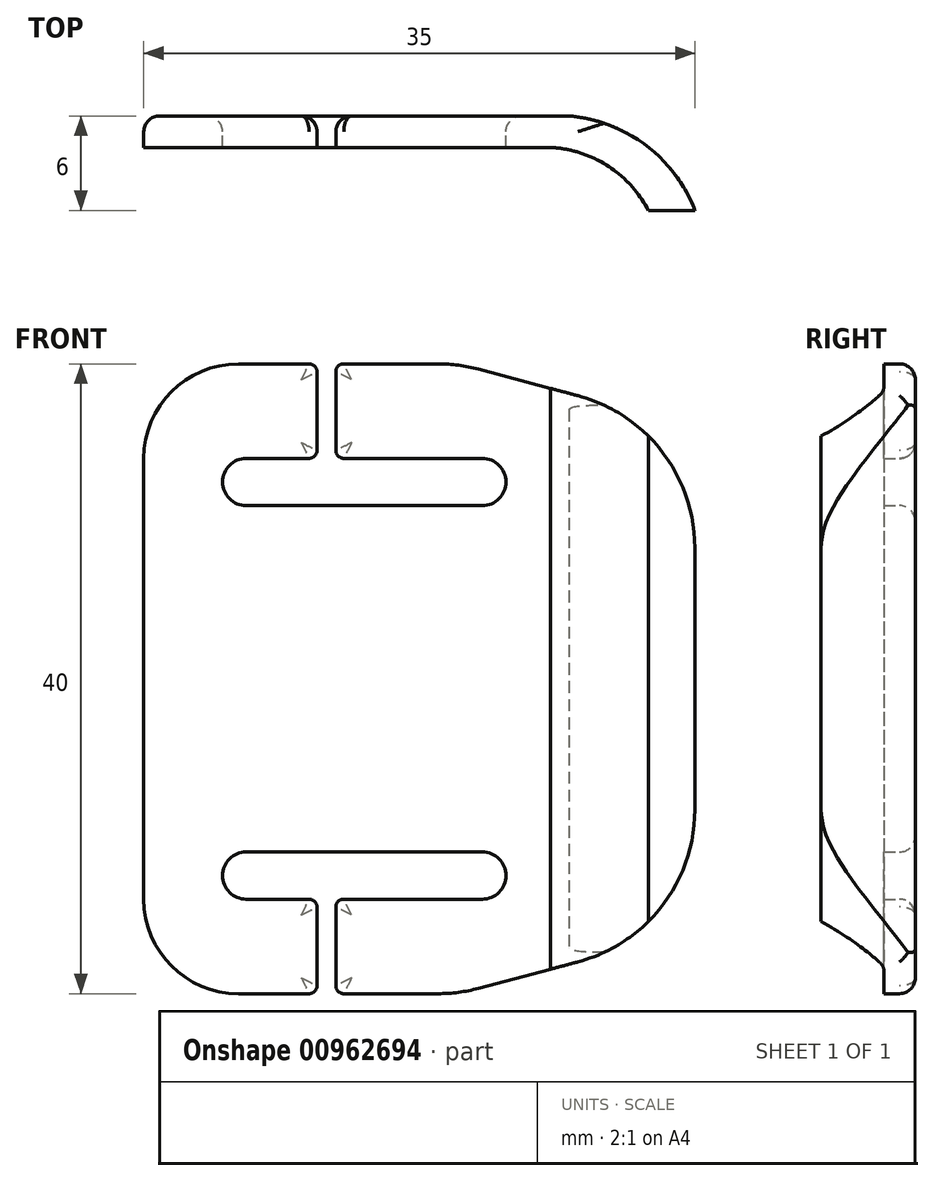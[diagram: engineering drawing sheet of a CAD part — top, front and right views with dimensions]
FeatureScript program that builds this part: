
annotation { "Feature Type Name" : "Feature", "Feature Type Description" : "" }
export const myFeature = defineFeature(function(context is Context, id is Id, definition is map)
    precondition{}
    {
        {
            var Q0;
            Q0=qCreatedBy(makeId("Front.planeOp"),FACE);
            var sketch = newSketch(context, id + "F0", { "sketchPlane" : qUnion([Q0])});
            skLineSegment(sketch, "E0.bottom", {"start": v(1, -20) * mm, "end": v(5.5, -20) * mm});
            skLineSegment(sketch, "E0.top", {"start": v(1, 20) * mm, "end": v(5.5, 20) * mm});
            skLineSegment(sketch, "E0.left", {"start": v(-5, -14) * mm, "end": v(-5, 14) * mm});
            skLineSegment(sketch, "E0.right", {"start": v(30, -8.32) * mm, "end": v(30, 8.32) * mm});
            skLineSegment(sketch, "E1.bottom", {"start": v(1.5, 14) * mm, "end": v(5.5, 14) * mm});
            skLineSegment(sketch, "E1.top", {"start": v(1.5, 11) * mm, "end": v(16.5, 11) * mm});
            skLineSegment(sketch, "E1.left", {"start": v(0, 12.5) * mm, "end": v(0, 12.5) * mm});
            skLineSegment(sketch, "E1.right", {"start": v(18, 12.5) * mm, "end": v(18, 12.5) * mm});
            skLineSegment(sketch, "E2.bottom", {"start": v(1.5, -11) * mm, "end": v(16.5, -11) * mm});
            skLineSegment(sketch, "E2.top", {"start": v(1.5, -14) * mm, "end": v(5.5, -14) * mm});
            skLineSegment(sketch, "E2.left", {"start": v(0, -12.5) * mm, "end": v(0, -12.5) * mm});
            skLineSegment(sketch, "E2.right", {"start": v(18, -12.5) * mm, "end": v(18, -12.5) * mm});
            skPoint(sketch, "E3.visualSharp", {"position": v(-5, 20) * mm});
            skArc(sketch, "E3.filletArc", {"start": v(1, 20) * mm, "mid": v(-3.24, 18.24) * mm, "end": v(-5, 14) * mm});
            skPoint(sketch, "E4.visualSharp", {"position": v(-5, -20) * mm});
            skArc(sketch, "E4.filletArc", {"start": v(-5, -14) * mm, "mid": v(-3.24, -18.24) * mm, "end": v(1, -20) * mm});
            skLineSegment(sketch, "E5", {"start": v(6, 19.5) * mm, "end": v(6, 14.5) * mm});
            skLineSegment(sketch, "E6", {"start": v(7.2, 19.5) * mm, "end": v(7.2, 14.5) * mm});
            skLineSegment(sketch, "E7.trimOffspring", {"start": v(6, -14.5) * mm, "end": v(6, -19.5) * mm});
            skLineSegment(sketch, "E8.trimOffspring", {"start": v(7.2, -14.5) * mm, "end": v(7.2, -19.5) * mm});
            skLineSegment(sketch, "E9.trimOffspring", {"start": v(7.7, -20) * mm, "end": v(13.69, -20) * mm});
            skLineSegment(sketch, "E10.trimOffspring", {"start": v(7.7, -14) * mm, "end": v(16.5, -14) * mm});
            skLineSegment(sketch, "E11.trimOffspring", {"start": v(7.7, 14) * mm, "end": v(16.5, 14) * mm});
            skLineSegment(sketch, "E12.trimOffspring", {"start": v(7.7, 20) * mm, "end": v(13.69, 20) * mm});
            skPoint(sketch, "E13.visualSharp", {"position": v(0, 14) * mm});
            skArc(sketch, "E13.filletArc", {"start": v(1.5, 14) * mm, "mid": v(0.44, 13.56) * mm, "end": v(0, 12.5) * mm});
            skPoint(sketch, "E14.visualSharp", {"position": v(0, 11) * mm});
            skArc(sketch, "E14.filletArc", {"start": v(0, 12.5) * mm, "mid": v(0.44, 11.44) * mm, "end": v(1.5, 11) * mm});
            skPoint(sketch, "E15.visualSharp", {"position": v(18, 14) * mm});
            skArc(sketch, "E15.filletArc", {"start": v(18, 12.5) * mm, "mid": v(17.56, 13.56) * mm, "end": v(16.5, 14) * mm});
            skPoint(sketch, "E16.visualSharp", {"position": v(18, 11) * mm});
            skArc(sketch, "E16.filletArc", {"start": v(16.5, 11) * mm, "mid": v(17.56, 11.44) * mm, "end": v(18, 12.5) * mm});
            skPoint(sketch, "E17.visualSharp", {"position": v(0, -11) * mm});
            skArc(sketch, "E17.filletArc", {"start": v(1.5, -11) * mm, "mid": v(0.44, -11.44) * mm, "end": v(0, -12.5) * mm});
            skPoint(sketch, "E18.visualSharp", {"position": v(0, -14) * mm});
            skArc(sketch, "E18.filletArc", {"start": v(0, -12.5) * mm, "mid": v(0.44, -13.56) * mm, "end": v(1.5, -14) * mm});
            skPoint(sketch, "E19.visualSharp", {"position": v(18, -11) * mm});
            skArc(sketch, "E19.filletArc", {"start": v(18, -12.5) * mm, "mid": v(17.56, -11.44) * mm, "end": v(16.5, -11) * mm});
            skPoint(sketch, "E20.visualSharp", {"position": v(18, -14) * mm});
            skArc(sketch, "E20.filletArc", {"start": v(16.5, -14) * mm, "mid": v(17.56, -13.56) * mm, "end": v(18, -12.5) * mm});
            skPoint(sketch, "E21.visualSharp", {"position": v(6, 14) * mm});
            skArc(sketch, "E21.filletArc", {"start": v(5.5, 14) * mm, "mid": v(5.85, 14.15) * mm, "end": v(6, 14.5) * mm});
            skPoint(sketch, "E22.visualSharp", {"position": v(7.2, 14) * mm});
            skArc(sketch, "E22.filletArc", {"start": v(7.2, 14.5) * mm, "mid": v(7.35, 14.15) * mm, "end": v(7.7, 14) * mm});
            skPoint(sketch, "E23.visualSharp", {"position": v(6, 20) * mm});
            skArc(sketch, "E23.filletArc", {"start": v(6, 19.5) * mm, "mid": v(5.85, 19.85) * mm, "end": v(5.5, 20) * mm});
            skPoint(sketch, "E24.visualSharp", {"position": v(7.2, 20) * mm});
            skArc(sketch, "E24.filletArc", {"start": v(7.7, 20) * mm, "mid": v(7.35, 19.85) * mm, "end": v(7.2, 19.5) * mm});
            skPoint(sketch, "E25.visualSharp", {"position": v(6, -20) * mm});
            skArc(sketch, "E25.filletArc", {"start": v(5.5, -20) * mm, "mid": v(5.85, -19.85) * mm, "end": v(6, -19.5) * mm});
            skPoint(sketch, "E26.visualSharp", {"position": v(7.2, -20) * mm});
            skArc(sketch, "E26.filletArc", {"start": v(7.2, -19.5) * mm, "mid": v(7.35, -19.85) * mm, "end": v(7.7, -20) * mm});
            skPoint(sketch, "E27.visualSharp", {"position": v(6, -14) * mm});
            skArc(sketch, "E27.filletArc", {"start": v(6, -14.5) * mm, "mid": v(5.85, -14.15) * mm, "end": v(5.5, -14) * mm});
            skPoint(sketch, "E28.visualSharp", {"position": v(7.2, -14) * mm});
            skArc(sketch, "E28.filletArc", {"start": v(7.7, -14) * mm, "mid": v(7.35, -14.15) * mm, "end": v(7.2, -14.5) * mm});
            skLineSegment(sketch, "E29", {"start": v(16.27, -19.66) * mm, "end": v(22.58, -17.98) * mm});
            skPoint(sketch, "E30.visualSharp", {"position": v(15, -20) * mm});
            skArc(sketch, "E30.filletArc", {"start": v(13.69, -20) * mm, "mid": v(14.99, -19.92) * mm, "end": v(16.27, -19.66) * mm});
            skPoint(sketch, "E31.visualSharp", {"position": v(30, -16) * mm});
            skArc(sketch, "E31.filletArc", {"start": v(22.58, -17.98) * mm, "mid": v(27.93, -14.4) * mm, "end": v(30, -8.32) * mm});
            skArc(sketch, "E32.MirrorCS", {"start": v(22.58, 17.98) * mm, "mid": v(27.93, 14.4) * mm, "end": v(30, 8.32) * mm});
            skLineSegment(sketch, "E33.MirrorCS", {"start": v(16.27, 19.66) * mm, "end": v(22.58, 17.98) * mm});
            skArc(sketch, "E34.MirrorCS", {"start": v(13.69, 20) * mm, "mid": v(14.99, 19.92) * mm, "end": v(16.27, 19.66) * mm});
            skSolve(sketch);
        }
        {
            var Q0;
            Q0=qSketchRegion(id+"F0",true);
            extrude(context, id + "F1", {"entities" : qUnion([Q0]), "depth" : 6 * mm, "offsetDistance" : 25 * mm});
        }
        {
            var Q0;
            Q0=makeQuery(id+"F1.opExtrude","SWEPT_FACE",FACE,{"disambiguationData":[OSD([sQuery(id+"F0.wireOp",EDGE,"E9.trimOffspring")])]});
            var sketch = newSketch(context, id + "F2", { "sketchPlane" : qUnion([Q0])});
            skLineSegment(sketch, "E35", {"start": v(-6.5, 2) * mm, "end": v(20.84, 2) * mm});
            skArc(sketch, "E36", {"start": v(20.84, 2) * mm, "mid": v(24.47, 3.17) * mm, "end": v(27.04, 6) * mm});
            skArc(sketch, "E37", {"start": v(22, 0) * mm, "mid": v(26.87, 1.85) * mm, "end": v(30, 6) * mm});
            skLineSegment(sketch, "E38", {"start": v(-7.66, 0) * mm, "end": v(22, 0) * mm});
            skPoint(sketch, "E39.orphan", {"position": v(30.17, 6) * mm});
            skPoint(sketch, "E40.orphan", {"position": v(-7.66, 0) * mm});
            skLineSegment(sketch, "E41", {"start": v(-6.5, 2) * mm, "end": v(-6.5, 8.41) * mm});
            skLineSegment(sketch, "E42", {"start": v(-6.5, 8.41) * mm, "end": v(27.04, 8.41) * mm});
            skLineSegment(sketch, "E43", {"start": v(27.04, 8.41) * mm, "end": v(27.04, 6) * mm});
            skLineSegment(sketch, "E44", {"start": v(-7.66, 0) * mm, "end": v(-7.66, -2.54) * mm});
            skLineSegment(sketch, "E45", {"start": v(-7.66, -2.54) * mm, "end": v(31.35, -2.54) * mm});
            skLineSegment(sketch, "E46", {"start": v(31.35, -2.54) * mm, "end": v(31.35, 6) * mm});
            skLineSegment(sketch, "E47", {"start": v(31.35, 6) * mm, "end": v(30, 6) * mm});
            skSolve(sketch);
        }
        {
            var Q0;
            {var subQ3=sQuery(id+"F2.wireOp",EDGE,"E37");Q0=makeQuery(id+"F2.imprint","IMPRINT",FACE,{"disambiguationData":[TD([[makeQuery(id+"F2.imprint","IMPRINT",EDGE,{"derivedFrom":subQ3}),-1.0]])]});}
            var Q1;
            {var subQ6=sQuery(id+"F2.wireOp",EDGE,"E36");Q1=makeQuery(id+"F2.imprint","IMPRINT",FACE,{"disambiguationData":[TD([[makeQuery(id+"F2.imprint","IMPRINT",EDGE,{"derivedFrom":subQ6}),1.0]])]});}
            var Q2;
            {var subQ1=sQuery(id+"F0.wireOp",EDGE,"E9.trimOffspring");var subQ6=makeQuery(id+"F1.opExtrude","CAP_EDGE",EDGE,{"disambiguationData":[OSD([subQ1])],"isStart":false});Q2=makeQuery(id+"F2.imprint","IMPRINT",FACE,{"disambiguationData":[TD([[makeQuery(id+"F2.imprint","IMPRINT",EDGE,{"derivedFrom":subQ6}),-1.0]])]});}
            var Q3;
            Q3=sQuery(id+"F2.wireOp",EDGE,"E38");
            extrude(context, id + "F3", {"entities" : qUnion([Q0, Q1, Q2]), "operationType" : NewBodyOperationType.REMOVE, "surfaceEntities" : qUnion([Q3]), "endBound" : BoundingType.THROUGH_ALL, "oppositeDirection" : true, "depth" : 100 * mm, "offsetDistance" : 25 * mm});
        }
        {
            var Q0;
            Q0=makeQuery(id+"F1.opExtrude","CAP_EDGE",EDGE,{"disambiguationData":[OSD([sQuery(id+"F0.wireOp",EDGE,"E0.left")])],"isStart":true});
            fillet(context, id + "F4", {"entities" : qUnion([Q0]), "radius" : 1 * mm, "tangentPropagation" : true, "allowEdgeOverflow" : false});
        }
    });
